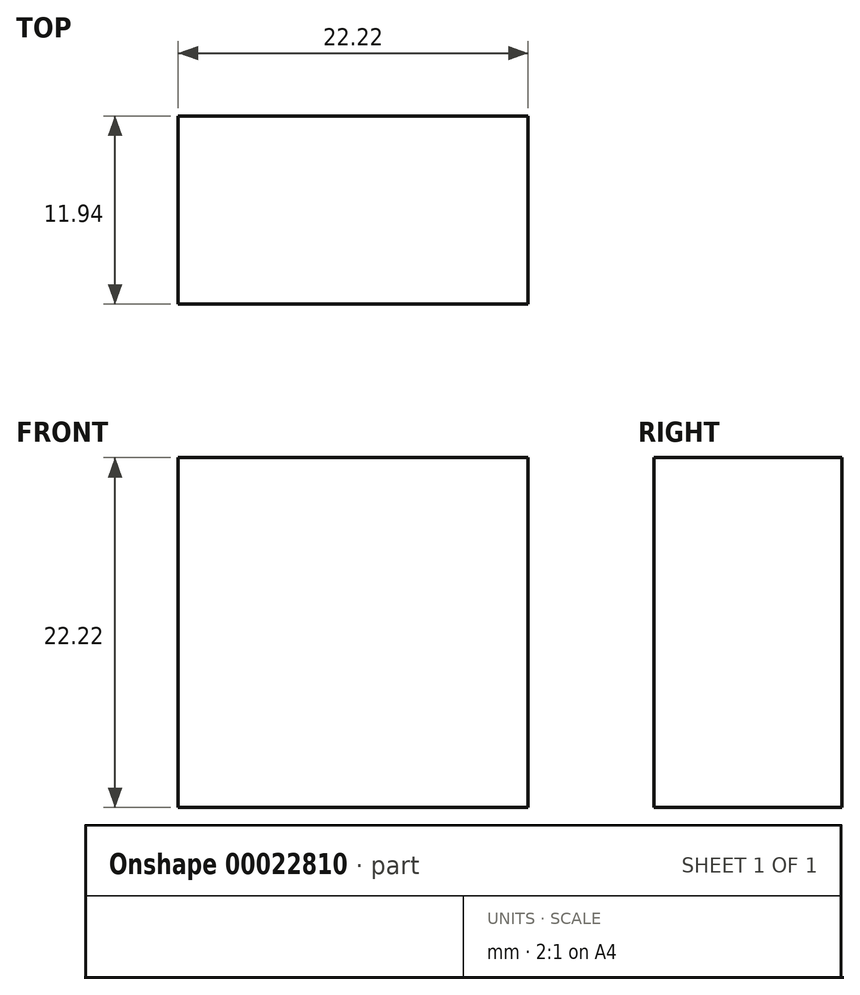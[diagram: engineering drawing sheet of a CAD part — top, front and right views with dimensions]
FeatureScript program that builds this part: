
annotation { "Feature Type Name" : "Feature", "Feature Type Description" : "" }
export const myFeature = defineFeature(function(context is Context, id is Id, definition is map)
    precondition{}
    {
        {
            var Q0;
            Q0=qCreatedBy(makeId("Front.planeOp"),FACE);
            var sketch = newSketch(context, id + "F0", { "sketchPlane" : qUnion([Q0])});
            skLineSegment(sketch, "E0.bottom", {"start": v(11.92, 9.37) * mm, "end": v(34.14, 9.37) * mm});
            skLineSegment(sketch, "E0.top", {"start": v(11.92, -12.85) * mm, "end": v(34.14, -12.85) * mm});
            skLineSegment(sketch, "E0.left", {"start": v(11.92, 9.37) * mm, "end": v(11.92, -12.85) * mm});
            skLineSegment(sketch, "E0.right", {"start": v(34.14, 9.37) * mm, "end": v(34.14, -12.85) * mm});
            skSolve(sketch);
        }
        {
            var Q0;
            Q0=makeQuery(id+"F0.imprint","IMPRINT",FACE,{"disambiguationData":[TD([[makeQuery(id+"F0.imprint","IMPRINT",EDGE,{"derivedFrom":sQuery(id+"F0.wireOp",EDGE,"E0.bottom")}),-1.0]])]});
            extrude(context, id + "F1", {"entities" : qUnion([Q0]), "depth" : 11.94 * mm});
        }
    });
